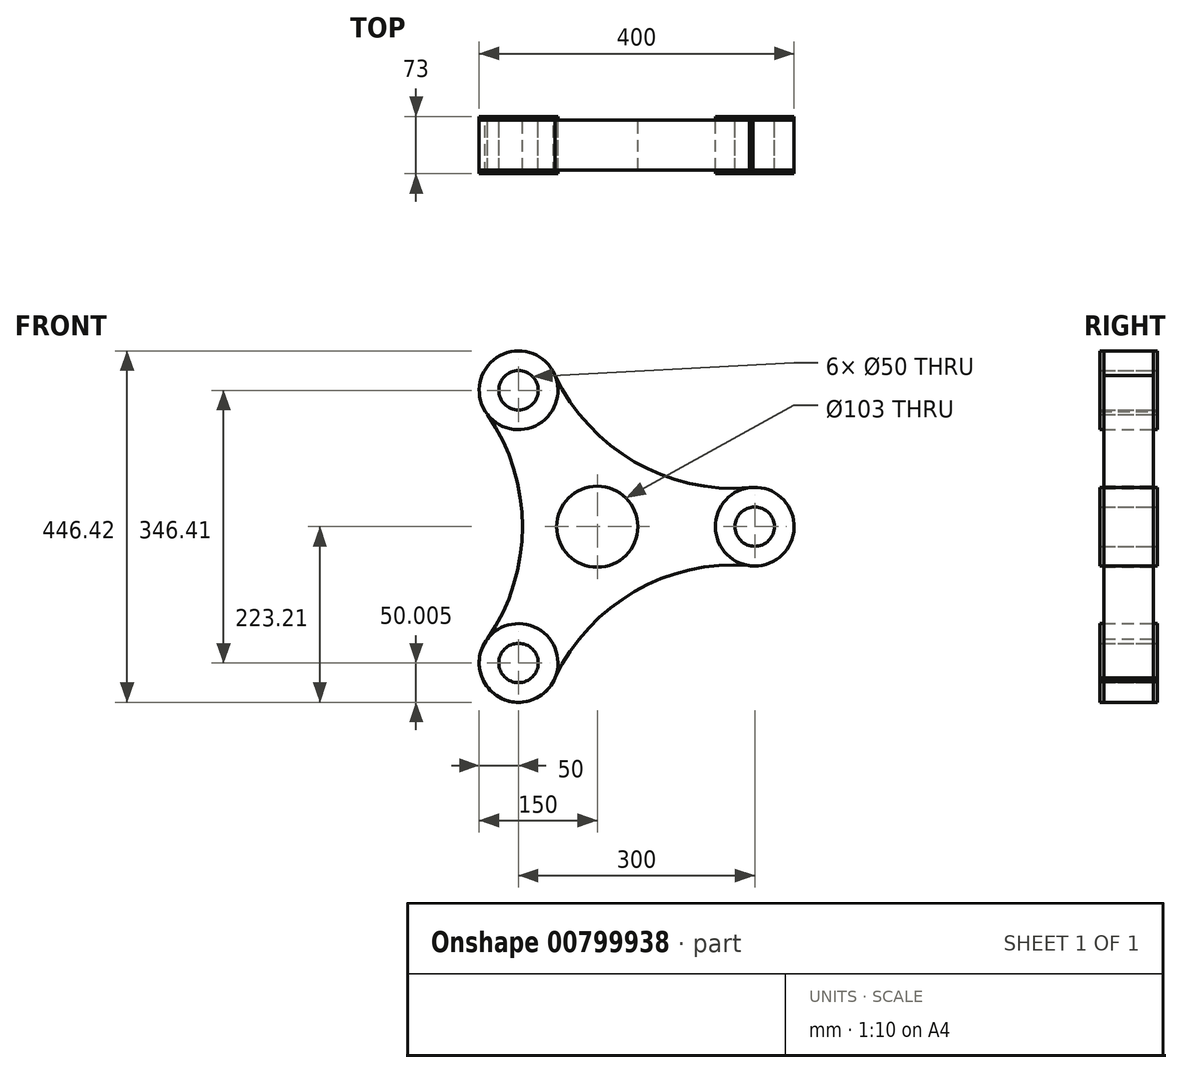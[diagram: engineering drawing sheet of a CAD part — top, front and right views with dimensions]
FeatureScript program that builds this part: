
annotation { "Feature Type Name" : "Feature", "Feature Type Description" : "" }
export const myFeature = defineFeature(function(context is Context, id is Id, definition is map)
    precondition{}
    {
        {
            var Q0;
            Q0=qCreatedBy(makeId("Front.planeOp"),FACE);
            var sketch = newSketch(context, id + "F0", { "sketchPlane" : qUnion([Q0])});
            skCircle(sketch, "E0", {"center": v(200, 0) * mm, "radius": 25 * mm});
            skCircle(sketch, "E1", {"center": v(0, 0) * mm, "radius": 51.5 * mm});
            skCircle(sketch, "E2", {"center": v(200, 0) * mm, "radius": 50 * mm});
            skCircle(sketch, "E3.1.0", {"center": v(-100, 173.2) * mm, "radius": 50 * mm});
            skCircle(sketch, "E3.1.1", {"center": v(-100, 173.2) * mm, "radius": 25 * mm});
            skCircle(sketch, "E3.2.0", {"center": v(-100, -173.2) * mm, "radius": 50 * mm});
            skCircle(sketch, "E3.2.1", {"center": v(-100, -173.2) * mm, "radius": 25 * mm});
            skArc(sketch, "E4", {"start": v(-142.29, 146.53) * mm, "mid": v(-95.08, 2.53) * mm, "end": v(-139.37, -142.39) * mm});
            skArc(sketch, "E5.1.0", {"start": v(-55.75, -196.49) * mm, "mid": v(45.35, -83.6) * mm, "end": v(193, -49.5) * mm});
            skArc(sketch, "E5.2.0", {"start": v(198.04, 49.96) * mm, "mid": v(49.73, 81.07) * mm, "end": v(-53.62, 191.9) * mm});
            skSolve(sketch);
        }
        {
            var Q0;
            Q0=makeQuery(id+"F0.imprint","IMPRINT",FACE,{"disambiguationData":[TD([[makeQuery(id+"F0.imprint","IMPRINT",EDGE,{"derivedFrom":sQuery(id+"F0.wireOp",EDGE,"E0")}),-1.0]])]});
            var Q1;
            Q1=makeQuery(id+"F0.imprint","IMPRINT",FACE,{"disambiguationData":[TD([[makeQuery(id+"F0.imprint","IMPRINT",EDGE,{"derivedFrom":sQuery(id+"F0.wireOp",EDGE,"E3.2.0")}),1.0]])]});
            var Q2;
            Q2=makeQuery(id+"F0.imprint","IMPRINT",FACE,{"disambiguationData":[TD([[makeQuery(id+"F0.imprint","IMPRINT",EDGE,{"derivedFrom":sQuery(id+"F0.wireOp",EDGE,"E3.1.0")}),1.0]])]});
            extrude(context, id + "F1", {"entities" : qUnion([Q0, Q1, Q2]), "endBound" : BoundingType.SYMMETRIC, "depth" : 73 * mm, "offsetDistance" : 25 * mm});
        }
        {
            var Q0;
            Q0 = qSketchRegion(id + "F0", true);
            extrude(context, id + "F2", {"entities" : qUnion([Q0]), "endBound" : BoundingType.SYMMETRIC, "depth" : 63 * mm, "offsetDistance" : 25 * mm});
        }
    });
